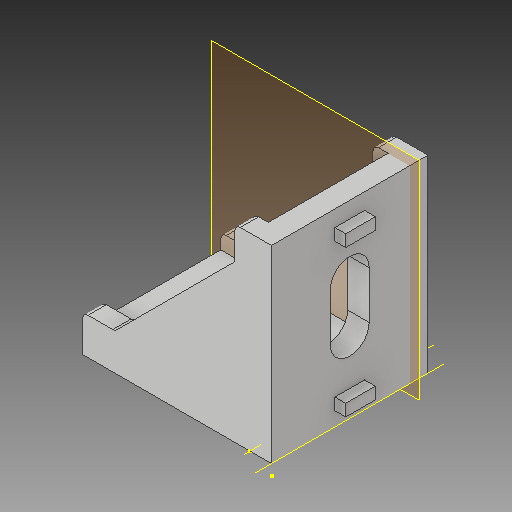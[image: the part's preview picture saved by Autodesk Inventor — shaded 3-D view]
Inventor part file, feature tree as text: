
AUTODESK INVENTOR PART (.ipt)
format: ipt  version: 2017 (Build 210142000, 142)  size: 181,248 bytes
history: native  units: mm
features: sketch x8, other x5, plane x1
ambient origin geometry x8: Origin, YZ Plane, XZ Plane, XY Plane, X Axis, Y Axis, Z Axis, Center Point
bodies: Solid1 (feature_tree)
feature tree (14):
  other  "30mm Bracket_CPY_MIR2_MIR1.ipt"
  other  "Solid1::30mm Bracket_CPY_MIR2_MIR1.ipt"
  other  "TaggingFeature1"
  sketch  "Sketch1"  dims[d0=10.0mm]
  sketch  "Sketch2"
  sketch  "Sketch3"
  sketch  "Sketch4"
  sketch  "Sketch5"
  sketch  "Sketch7"
  sketch  "Sketch9"
  sketch  "Sketch10"
  plane  "Work Plane1"
  other  "Work Axis1"
  other  "Work Axis2"
